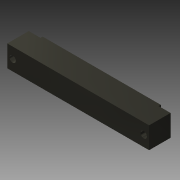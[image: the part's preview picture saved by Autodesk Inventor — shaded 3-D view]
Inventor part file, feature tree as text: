
AUTODESK INVENTOR PART (.ipt)
format: ipt  version: 2013 (Build 170138000, 138)  size: 107,008 bytes
history: native  units: mm
features: sketch x4, extrude x3, other x1, hole x1
ambient origin geometry x8: Origin, YZ Plane, XZ Plane, XY Plane, X Axis, Y Axis, Z Axis, Center Point
feature tree (9):
  other  "ソリッド1"
  extrude  "押し出し1"  Depth=70.0mm
  hole  "穴1"  [1 undecoded]
  extrude  "押し出し15"  Depth=10.0mm TaperAngle=0.0deg
  extrude  "押し出し16"  Depth=4.5mm
  sketch  "スケッチ1"
  sketch  "スケッチ17"
  sketch  "スケッチ18"
  sketch  "スケッチ19"
note: 1 required parameter value undecoded (feature->parameter linkage not recoverable at this tier; creation-order binding heuristic only, values carry confidence <= 0.55)
